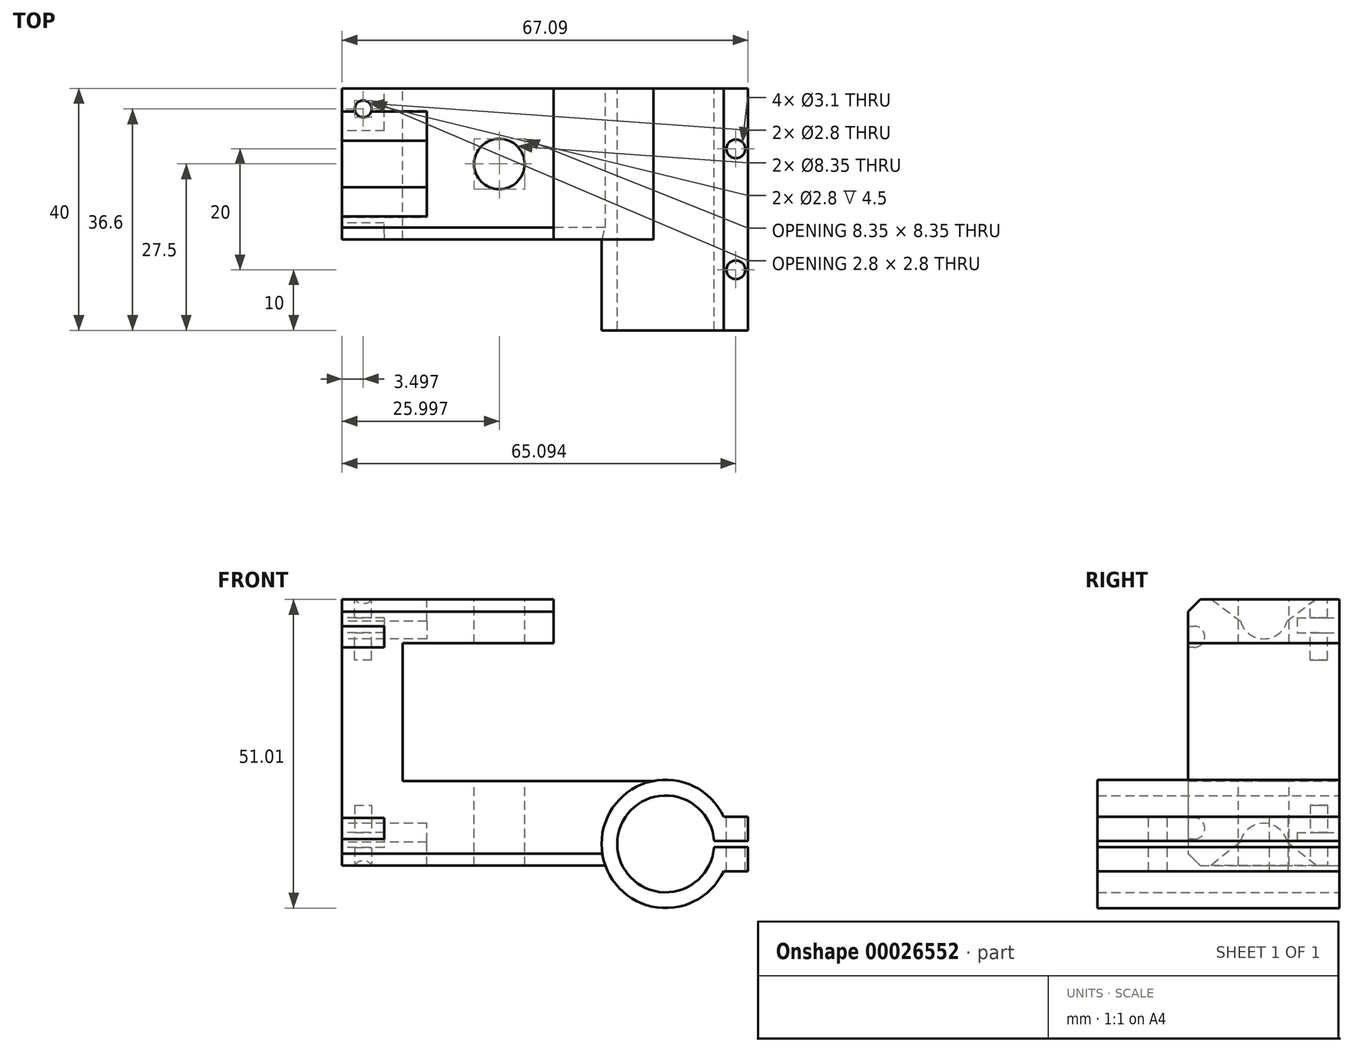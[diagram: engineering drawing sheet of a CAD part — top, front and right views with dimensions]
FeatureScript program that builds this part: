
annotation { "Feature Type Name" : "Feature", "Feature Type Description" : "" }
export const myFeature = defineFeature(function(context is Context, id is Id, definition is map)
    precondition{}
    {
        {
            var Q0;
            Q0=qCreatedBy(makeId("Front.planeOp"),FACE);
            var sketch = newSketch(context, id + "F0", { "sketchPlane" : qUnion([Q0])});
            skLineSegment(sketch, "E0", {"start": v(-4.26, -3.6) * mm, "end": v(29.26, -3.6) * mm});
            skLineSegment(sketch, "E1", {"start": v(37.24, 10.4) * mm, "end": v(-4.26, 10.4) * mm});
            skLineSegment(sketch, "E2", {"start": v(-4.26, 40.4) * mm, "end": v(-14.26, 40.4) * mm});
            skLineSegment(sketch, "E3", {"start": v(-14.26, 40.4) * mm, "end": v(-14.26, -3.6) * mm});
            skLineSegment(sketch, "E4", {"start": v(-14.26, -3.6) * mm, "end": v(-4.26, -3.6) * mm});
            skLineSegment(sketch, "E5", {"start": v(-4.26, 40.4) * mm, "end": v(20.74, 40.4) * mm});
            skLineSegment(sketch, "E6", {"start": v(20.74, 40.4) * mm, "end": v(20.74, 33.16) * mm});
            skLineSegment(sketch, "E7", {"start": v(20.74, 33.16) * mm, "end": v(-4.26, 33.16) * mm});
            skLineSegment(sketch, "E8", {"start": v(-4.26, 33.16) * mm, "end": v(-4.26, 10.4) * mm});
            skCircle(sketch, "E9", {"center": v(39.24, 0) * mm, "radius": 8 * mm});
            skCircle(sketch, "E10", {"center": v(39.24, 0) * mm, "radius": 10.6 * mm});
            skLineSegment(sketch, "E11", {"start": v(39.24, 0) * mm, "end": v(52.83, 0) * mm});
            skLineSegment(sketch, "E12", {"start": v(39.24, 0) * mm, "end": v(39.24, 0.5) * mm});
            skLineSegment(sketch, "E13", {"start": v(39.24, 0.5) * mm, "end": v(52.83, 0.5) * mm});
            skLineSegment(sketch, "E14", {"start": v(52.83, 0.5) * mm, "end": v(52.83, -0.5) * mm});
            skLineSegment(sketch, "E15", {"start": v(52.83, -0.5) * mm, "end": v(39.24, -0.5) * mm});
            skLineSegment(sketch, "E16", {"start": v(39.24, -0.5) * mm, "end": v(39.24, 0) * mm});
            skLineSegment(sketch, "E17", {"start": v(52.83, 0.5) * mm, "end": v(52.83, 4.5) * mm});
            skLineSegment(sketch, "E18", {"start": v(52.83, 4.5) * mm, "end": v(48.83, 4.5) * mm});
            skLineSegment(sketch, "E19", {"start": v(52.83, -0.5) * mm, "end": v(52.83, -4.5) * mm});
            skLineSegment(sketch, "E20", {"start": v(52.83, -4.5) * mm, "end": v(48.83, -4.5) * mm});
            skSolve(sketch);
        }
        {
            var Q0;
            Q0=makeQuery(id+"F0.imprint","IMPRINT",FACE,{"disambiguationData":[TD([[makeQuery(id+"F0.imprint","IMPRINT",EDGE,{"derivedFrom":sQuery(id+"F0.wireOp",EDGE,"E0")}),1.0]])]});
            extrude(context, id + "F1", {"entities" : qUnion([Q0]), "depth" : 25 * mm});
        }
        {
            var Q0;
            Q0=makeQuery(id+"F1.opExtrude","SWEPT_FACE",FACE,{"disambiguationData":[OSD([sQuery(id+"F0.wireOp",EDGE,"E3")])]});
            var sketch = newSketch(context, id + "F2", { "sketchPlane" : qUnion([Q0])});
            skLineSegment(sketch, "E21", {"start": v(12.5, 40.4) * mm, "end": v(12.5, -3.6) * mm, "construction": true});
            skCircle(sketch, "E22", {"center": v(12.5, 37.9) * mm, "radius": 4 * mm});
            skCircle(sketch, "E23", {"center": v(12.5, -0.6) * mm, "radius": 4 * mm});
            skCircle(sketch, "E24", {"center": v(24, 34.26) * mm, "radius": 1.75 * mm});
            skCircle(sketch, "E25", {"center": v(24, 2.56) * mm, "radius": 1.75 * mm});
            skLineSegment(sketch, "E26", {"start": v(24, 32.5) * mm, "end": v(25, 32.5) * mm});
            skLineSegment(sketch, "E27", {"start": v(25, 36) * mm, "end": v(24, 36) * mm});
            skLineSegment(sketch, "E28", {"start": v(24, 4.3) * mm, "end": v(25, 4.3) * mm});
            skLineSegment(sketch, "E29", {"start": v(24, 0.8) * mm, "end": v(25, 0.8) * mm});
            skSolve(sketch);
        }
        {
            var Q0;
            {var subQ0=makeQuery(id+"F1.opExtrude","SWEPT_EDGE",EDGE,{"disambiguationData":[OSD([sQuery(id+"F0.wireOp",EDGE,"E2"),sQuery(id+"F0.wireOp",EDGE,"E3")])]});var subQ1=sQuery(id+"F2.wireOp",EDGE,"E22");var subQ3=makeQuery(id+"F2.imprint","INTERSECT",VERTEX,{"disambiguationData":[OD(0.0)],"derivedFrom":[subQ0,subQ1]});Q0=makeQuery(id+"F2.imprint","IMPRINT",FACE,{"disambiguationData":[TD([[makeQuery(id+"F2.imprint","IMPRINT",EDGE,{"disambiguationData":[TD([[subQ3,1.0]])],"derivedFrom":subQ1}),1.0]])]});}
            var Q1;
            {var subQ0=makeQuery(id+"F1.opExtrude","SWEPT_EDGE",EDGE,{"disambiguationData":[OSD([sQuery(id+"F0.wireOp",EDGE,"E3"),sQuery(id+"F0.wireOp",EDGE,"E4")])]});var subQ1=sQuery(id+"F2.wireOp",EDGE,"E23");var subQ3=makeQuery(id+"F2.imprint","INTERSECT",VERTEX,{"disambiguationData":[OD(0.0)],"derivedFrom":[subQ0,subQ1]});Q1=makeQuery(id+"F2.imprint","IMPRINT",FACE,{"disambiguationData":[TD([[makeQuery(id+"F2.imprint","IMPRINT",EDGE,{"disambiguationData":[TD([[subQ3,-1.0]])],"derivedFrom":subQ1}),1.0]])]});}
            var Q2;
            {var subQ0=makeQuery(id+"F1.opExtrude","SWEPT_EDGE",EDGE,{"disambiguationData":[OSD([sQuery(id+"F0.wireOp",EDGE,"E2"),sQuery(id+"F0.wireOp",EDGE,"E3")])]});var subQ1=sQuery(id+"F2.wireOp",EDGE,"E22");var subQ3=makeQuery(id+"F2.imprint","INTERSECT",VERTEX,{"disambiguationData":[OD(0.0)],"derivedFrom":[subQ0,subQ1]});Q2=makeQuery(id+"F2.imprint","IMPRINT",FACE,{"disambiguationData":[TD([[makeQuery(id+"F2.imprint","IMPRINT",EDGE,{"disambiguationData":[TD([[subQ3,-1.0]])],"derivedFrom":subQ1}),1.0]])]});}
            var Q3;
            {var subQ0=makeQuery(id+"F1.opExtrude","SWEPT_EDGE",EDGE,{"disambiguationData":[OSD([sQuery(id+"F0.wireOp",EDGE,"E3"),sQuery(id+"F0.wireOp",EDGE,"E4")])]});var subQ1=sQuery(id+"F2.wireOp",EDGE,"E23");var subQ3=makeQuery(id+"F2.imprint","INTERSECT",VERTEX,{"disambiguationData":[OD(0.0)],"derivedFrom":[subQ0,subQ1]});Q3=makeQuery(id+"F2.imprint","IMPRINT",FACE,{"disambiguationData":[TD([[makeQuery(id+"F2.imprint","IMPRINT",EDGE,{"disambiguationData":[TD([[subQ3,1.0]])],"derivedFrom":subQ1}),1.0]])]});}
            extrude(context, id + "F3", {"entities" : qUnion([Q0, Q1, Q2, Q3]), "operationType" : NewBodyOperationType.REMOVE, "oppositeDirection" : true, "depth" : 14 * mm});
        }
        {
            var Q0;
            {var subQ1=sQuery(id+"F0.wireOp",EDGE,"E9");var subQ5=sQuery(id+"F0.wireOp",EDGE,"E13");var subQ6=makeQuery(id+"F0.imprint","INTERSECT",VERTEX,{"derivedFrom":[subQ1,subQ5]});Q0=makeQuery(id+"F0.imprint","IMPRINT",FACE,{"disambiguationData":[TD([[makeQuery(id+"F0.imprint","IMPRINT",EDGE,{"disambiguationData":[TD([[subQ6,-1.0]])],"derivedFrom":subQ1}),-1.0]])]});}
            var Q1;
            {var subQ1=sQuery(id+"F0.wireOp",EDGE,"E17");Q1=makeQuery(id+"F0.imprint","IMPRINT",FACE,{"disambiguationData":[TD([[makeQuery(id+"F0.imprint","IMPRINT",EDGE,{"derivedFrom":subQ1}),1.0]])]});}
            var Q2;
            {var subQ0=sQuery(id+"F0.wireOp",EDGE,"E19");Q2=makeQuery(id+"F0.imprint","IMPRINT",FACE,{"disambiguationData":[TD([[makeQuery(id+"F0.imprint","IMPRINT",EDGE,{"derivedFrom":subQ0}),-1.0]])]});}
            extrude(context, id + "F4", {"entities" : qUnion([Q0, Q1, Q2]), "operationType" : NewBodyOperationType.ADD, "depth" : 40 * mm});
        }
        {
            var Q0;
            Q0=makeQuery(id+"F1.opExtrude","SWEPT_FACE",FACE,{"disambiguationData":[OSD([sQuery(id+"F0.wireOp",EDGE,"E5")])]});
            var sketch = newSketch(context, id + "F5", { "sketchPlane" : qUnion([Q0])});
            skCircle(sketch, "E30", {"center": v(11.74, -12.5) * mm, "radius": 4.17 * mm});
            skLineSegment(sketch, "E31", {"start": v(20.74, -12.5) * mm, "end": v(11.74, -12.5) * mm});
            skSolve(sketch);
        }
        {
            var Q0;
            Q0=qSketchRegion(id+"F5",true);
            extrude(context, id + "F6", {"entities" : qUnion([Q0]), "operationType" : NewBodyOperationType.REMOVE, "endBound" : BoundingType.THROUGH_ALL, "oppositeDirection" : true, "depth" : 25 * mm});
        }
        {
            var Q0;
            Q0=makeQuery(id+"F1.opExtrude","SWEPT_FACE",FACE,{"disambiguationData":[OSD([sQuery(id+"F0.wireOp",EDGE,"E1")])]});
            var sketch = newSketch(context, id + "F7", { "sketchPlane" : qUnion([Q0])});
            skCircle(sketch, "E32", {"center": v(11.74, -12.5) * mm, "radius": 4.68 * mm});
            skCircle(sketch, "E33", {"center": v(11.74, -12.5) * mm, "radius": 4.17 * mm});
            skSolve(sketch);
        }
        {
            var Q0;
            Q0=makeQuery(id+"F1.opExtrude","SWEPT_FACE",FACE,{"disambiguationData":[OSD([sQuery(id+"F0.wireOp",EDGE,"E7")])]});
            var sketch = newSketch(context, id + "F8", { "sketchPlane" : qUnion([Q0])});
            skCircle(sketch, "E34", {"center": v(11.74, 12.5) * mm, "radius": 4.68 * mm});
            skCircle(sketch, "E35", {"center": v(11.74, 12.5) * mm, "radius": 4.17 * mm});
            skSolve(sketch);
        }
        {
            var Q0;
            Q0=makeQuery(id+"F1.opExtrude","CAP_EDGE",EDGE,{"disambiguationData":[OSD([sQuery(id+"F0.wireOp",EDGE,"E4")])],"isStart":false});
            var Q1;
            Q1=makeQuery(id+"F1.opExtrude","CAP_EDGE",EDGE,{"disambiguationData":[OSD([sQuery(id+"F0.wireOp",EDGE,"E2")])],"isStart":false});
            chamfer(context, id + "F9", {"entities" : qUnion([Q0, Q1]), "width" : 2 * mm, "tangentPropagation" : true});
        }
        {
            var Q0;
            Q0=makeQuery(id+"F3.boolean.opBoolean","INTERSECT",EDGE,{"disambiguationData":[OD(0.0)],"derivedFrom":[makeQuery(id+"F1.opExtrude","SWEPT_FACE",FACE,{"disambiguationData":[OSD([sQuery(id+"F0.wireOp",EDGE,"E4")])]}),makeQuery(id+"F3.opExtrude","SWEPT_FACE",FACE,{"disambiguationData":[OSD([sQuery(id+"F2.wireOp",EDGE,"E23")])]})]});
            var Q1;
            Q1=makeQuery(id+"F3.boolean.opBoolean","INTERSECT",EDGE,{"disambiguationData":[OD(1.0)],"derivedFrom":[makeQuery(id+"F1.opExtrude","SWEPT_FACE",FACE,{"disambiguationData":[OSD([sQuery(id+"F0.wireOp",EDGE,"E4")])]}),makeQuery(id+"F3.opExtrude","SWEPT_FACE",FACE,{"disambiguationData":[OSD([sQuery(id+"F2.wireOp",EDGE,"E23")])]})]});
            var Q2;
            Q2=makeQuery(id+"F3.boolean.opBoolean","INTERSECT",EDGE,{"disambiguationData":[OD(0.0)],"derivedFrom":[makeQuery(id+"F1.opExtrude","SWEPT_FACE",FACE,{"disambiguationData":[OSD([sQuery(id+"F0.wireOp",EDGE,"E2")])]}),makeQuery(id+"F3.opExtrude","SWEPT_FACE",FACE,{"disambiguationData":[OSD([sQuery(id+"F2.wireOp",EDGE,"E22")])]})]});
            var Q3;
            Q3=makeQuery(id+"F3.boolean.opBoolean","INTERSECT",EDGE,{"disambiguationData":[OD(1.0)],"derivedFrom":[makeQuery(id+"F1.opExtrude","SWEPT_FACE",FACE,{"disambiguationData":[OSD([sQuery(id+"F0.wireOp",EDGE,"E2")])]}),makeQuery(id+"F3.opExtrude","SWEPT_FACE",FACE,{"disambiguationData":[OSD([sQuery(id+"F2.wireOp",EDGE,"E22")])]})]});
            chamfer(context, id + "F10", {"entities" : qUnion([Q0, Q1, Q2, Q3]), "width" : 5 * mm, "tangentPropagation" : true});
        }
        {
            var Q0;
            {var subQ0=sQuery(id+"F0.wireOp",EDGE,"E2");var subQ1=sQuery(id+"F0.wireOp",EDGE,"57f85259-2936-4218-9d99-2fef228cf406");var subQ2=sQuery(id+"F0.wireOp",EDGE,"E3");Q0=makeQuery(id+"F3.boolean.opBoolean","SPLIT",FACE,{"disambiguationData":[TD([makeQuery(id+"F1.opExtrude","CAP_FACE",FACE,{"disambiguationData":[OSD([sQuery(id+"F0.wireOp",EDGE,"E0"),sQuery(id+"F0.wireOp",EDGE,"E1"),subQ0,subQ2,sQuery(id+"F0.wireOp",EDGE,"E4"),sQuery(id+"F0.wireOp",EDGE,"44816fb0-be7f-49fa-b092-a53b9556396f"),subQ1,sQuery(id+"F0.wireOp",EDGE,"E5"),sQuery(id+"F0.wireOp",EDGE,"E6"),sQuery(id+"F0.wireOp",EDGE,"E7"),sQuery(id+"F0.wireOp",EDGE,"E8"),sQuery(id+"F0.wireOp",EDGE,"E10")])],"isStart":true})])],"derivedFrom":makeQuery(id+"F1.opExtrude","SWEPT_FACE",FACE,{"disambiguationData":[OSD([subQ0])]})});}
            var sketch = newSketch(context, id + "F11", { "sketchPlane" : qUnion([Q0])});
            skCircle(sketch, "E36", {"center": v(-10.76, -3.4) * mm, "radius": 1.4 * mm});
            skLineSegment(sketch, "E37", {"start": v(-14.26, -3.4) * mm, "end": v(-7.26, -3.4) * mm});
            skLineSegment(sketch, "E38", {"start": v(-7.26, -7.27) * mm, "end": v(-7.26, 0) * mm});
            skSolve(sketch);
        }
        {
            var Q0;
            Q0=qSketchRegion(id+"F11",true);
            extrude(context, id + "F12", {"entities" : qUnion([Q0]), "operationType" : NewBodyOperationType.REMOVE, "oppositeDirection" : true, "depth" : 10 * mm});
        }
        {
            var Q0;
            {var subQ0=sQuery(id+"F0.wireOp",EDGE,"E4");var subQ1=sQuery(id+"F0.wireOp",EDGE,"44816fb0-be7f-49fa-b092-a53b9556396f");var subQ2=sQuery(id+"F0.wireOp",EDGE,"E3");Q0=makeQuery(id+"F3.boolean.opBoolean","SPLIT",FACE,{"disambiguationData":[TD([makeQuery(id+"F1.opExtrude","CAP_FACE",FACE,{"disambiguationData":[OSD([sQuery(id+"F0.wireOp",EDGE,"E0"),sQuery(id+"F0.wireOp",EDGE,"E1"),sQuery(id+"F0.wireOp",EDGE,"E2"),subQ2,subQ0,subQ1,sQuery(id+"F0.wireOp",EDGE,"57f85259-2936-4218-9d99-2fef228cf406"),sQuery(id+"F0.wireOp",EDGE,"E5"),sQuery(id+"F0.wireOp",EDGE,"E6"),sQuery(id+"F0.wireOp",EDGE,"E7"),sQuery(id+"F0.wireOp",EDGE,"E8"),sQuery(id+"F0.wireOp",EDGE,"E10")])],"isStart":true})])],"derivedFrom":makeQuery(id+"F1.opExtrude","SWEPT_FACE",FACE,{"disambiguationData":[OSD([subQ0])]})});}
            var sketch = newSketch(context, id + "F13", { "sketchPlane" : qUnion([Q0])});
            skCircle(sketch, "E39", {"center": v(-10.76, 3.4) * mm, "radius": 1.4 * mm});
            skLineSegment(sketch, "E40", {"start": v(-14.26, 3.4) * mm, "end": v(-14.26, 3.4) * mm});
            skLineSegment(sketch, "E41", {"start": v(-7.26, 7.27) * mm, "end": v(-7.26, 0) * mm});
            skLineSegment(sketch, "E42", {"start": v(-7.26, 3.4) * mm, "end": v(-14.26, 3.4) * mm});
            skSolve(sketch);
        }
        {
            var Q0;
            Q0=qSketchRegion(id+"F13",true);
            extrude(context, id + "F14", {"entities" : qUnion([Q0]), "operationType" : NewBodyOperationType.REMOVE, "oppositeDirection" : true, "depth" : 10 * mm});
        }
        {
            var Q0;
            Q0=makeQuery(id+"F4.opExtrude","SWEPT_FACE",FACE,{"disambiguationData":[OSD([sQuery(id+"F0.wireOp",EDGE,"E18")])]});
            var sketch = newSketch(context, id + "F15", { "sketchPlane" : qUnion([Q0])});
            skCircle(sketch, "E43", {"center": v(50.83, -10) * mm, "radius": 1.55 * mm});
            skLineSegment(sketch, "E44", {"start": v(52.83, -20) * mm, "end": v(50.83, -20) * mm});
            skLineSegment(sketch, "E45", {"start": v(50.83, 0) * mm, "end": v(50.83, -20) * mm});
            skLineSegment(sketch, "E46", {"start": v(50.83, -40) * mm, "end": v(50.83, -20) * mm});
            skCircle(sketch, "E47", {"center": v(50.83, -30) * mm, "radius": 1.55 * mm});
            skSolve(sketch);
        }
        {
            var Q0;
            Q0=qSketchRegion(id+"F15",true);
            extrude(context, id + "F16", {"entities" : qUnion([Q0]), "operationType" : NewBodyOperationType.REMOVE, "oppositeDirection" : true, "depth" : 25 * mm});
        }
        {
            var Q0;
            {var subQ1=sQuery(id+"F2.wireOp",EDGE,"E24");var subQ5=makeQuery(id+"F2.imprint","INTERSECT",VERTEX,{"derivedFrom":[subQ1,sQuery(id+"F2.wireOp",EDGE,"E27")]});Q0=makeQuery(id+"F2.imprint","IMPRINT",FACE,{"disambiguationData":[TD([[makeQuery(id+"F2.imprint","IMPRINT",EDGE,{"disambiguationData":[TD([[subQ5,1.0]])],"derivedFrom":subQ1}),1.0]])]});}
            var Q1;
            {var subQ1=sQuery(id+"F2.wireOp",EDGE,"E25");var subQ5=makeQuery(id+"F2.imprint","INTERSECT",VERTEX,{"derivedFrom":[subQ1,sQuery(id+"F2.wireOp",EDGE,"E28")]});Q1=makeQuery(id+"F2.imprint","IMPRINT",FACE,{"disambiguationData":[TD([[makeQuery(id+"F2.imprint","IMPRINT",EDGE,{"disambiguationData":[TD([[subQ5,1.0]])],"derivedFrom":subQ1}),1.0]])]});}
            var Q2;
            {var subQ3=sQuery(id+"F2.wireOp",EDGE,"E29");Q2=makeQuery(id+"F2.imprint","IMPRINT",FACE,{"disambiguationData":[TD([[makeQuery(id+"F2.imprint","IMPRINT",EDGE,{"derivedFrom":subQ3}),1.0]])]});}
            var Q3;
            {var subQ3=sQuery(id+"F2.wireOp",EDGE,"E28");Q3=makeQuery(id+"F2.imprint","IMPRINT",FACE,{"disambiguationData":[TD([[makeQuery(id+"F2.imprint","IMPRINT",EDGE,{"derivedFrom":subQ3}),-1.0]])]});}
            var Q4;
            {var subQ3=sQuery(id+"F2.wireOp",EDGE,"E27");Q4=makeQuery(id+"F2.imprint","IMPRINT",FACE,{"disambiguationData":[TD([[makeQuery(id+"F2.imprint","IMPRINT",EDGE,{"derivedFrom":subQ3}),1.0]])]});}
            var Q5;
            {var subQ3=sQuery(id+"F2.wireOp",EDGE,"E26");Q5=makeQuery(id+"F2.imprint","IMPRINT",FACE,{"disambiguationData":[TD([[makeQuery(id+"F2.imprint","IMPRINT",EDGE,{"derivedFrom":subQ3}),1.0]])]});}
            extrude(context, id + "F17", {"entities" : qUnion([Q0, Q1, Q2, Q3, Q4, Q5]), "operationType" : NewBodyOperationType.REMOVE, "oppositeDirection" : true, "depth" : 7 * mm});
        }
        {
            var Q0;
            {var subQ0=sQuery(id+"F0.wireOp",EDGE,"E10");Q0=makeQuery(id+"F4.boolean.opBoolean","MERGE",FACE,{"derivedFrom":[makeQuery(id+"F1.opExtrude","CAP_FACE",FACE,{"disambiguationData":[OSD([sQuery(id+"F0.wireOp",EDGE,"E0"),sQuery(id+"F0.wireOp",EDGE,"E1"),sQuery(id+"F0.wireOp",EDGE,"E2"),sQuery(id+"F0.wireOp",EDGE,"E3"),sQuery(id+"F0.wireOp",EDGE,"E4"),sQuery(id+"F0.wireOp",EDGE,"E5"),sQuery(id+"F0.wireOp",EDGE,"E6"),sQuery(id+"F0.wireOp",EDGE,"E7"),sQuery(id+"F0.wireOp",EDGE,"E8"),subQ0])],"isStart":true}),makeQuery(id+"F4.opExtrude","CAP_FACE",FACE,{"disambiguationData":[OSD([sQuery(id+"F0.wireOp",EDGE,"E9"),subQ0,sQuery(id+"F0.wireOp",EDGE,"E13"),sQuery(id+"F0.wireOp",EDGE,"E15"),sQuery(id+"F0.wireOp",EDGE,"E17"),sQuery(id+"F0.wireOp",EDGE,"E18"),sQuery(id+"F0.wireOp",EDGE,"E19"),sQuery(id+"F0.wireOp",EDGE,"E20")])],"isStart":true})]});}
            var sketch = newSketch(context, id + "F18", { "sketchPlane" : qUnion([Q0])});
            skLineSegment(sketch, "E48.bottom", {"start": v(7.26, 34.9) * mm, "end": v(14.26, 34.9) * mm});
            skLineSegment(sketch, "E48.top", {"start": v(7.26, 37.4) * mm, "end": v(14.26, 37.4) * mm});
            skLineSegment(sketch, "E48.left", {"start": v(7.26, 37.4) * mm, "end": v(7.26, 34.9) * mm});
            skLineSegment(sketch, "E48.right", {"start": v(14.26, 37.4) * mm, "end": v(14.26, 34.9) * mm});
            skLineSegment(sketch, "E49.bottom", {"start": v(7.26, 1.9) * mm, "end": v(14.26, 1.9) * mm});
            skLineSegment(sketch, "E49.top", {"start": v(7.26, -0.6) * mm, "end": v(14.26, -0.6) * mm});
            skLineSegment(sketch, "E49.left", {"start": v(7.26, 1.9) * mm, "end": v(7.26, -0.6) * mm});
            skLineSegment(sketch, "E49.right", {"start": v(14.26, 1.9) * mm, "end": v(14.26, -0.6) * mm});
            skPoint(sketch, "E50", {"position": v(10.76, 37.4) * mm});
            skSolve(sketch);
        }
        {
            var Q0;
            Q0=qSketchRegion(id+"F18",true);
            extrude(context, id + "F19", {"entities" : qUnion([Q0]), "operationType" : NewBodyOperationType.REMOVE, "oppositeDirection" : true, "depth" : 7 * mm});
        }
    });
